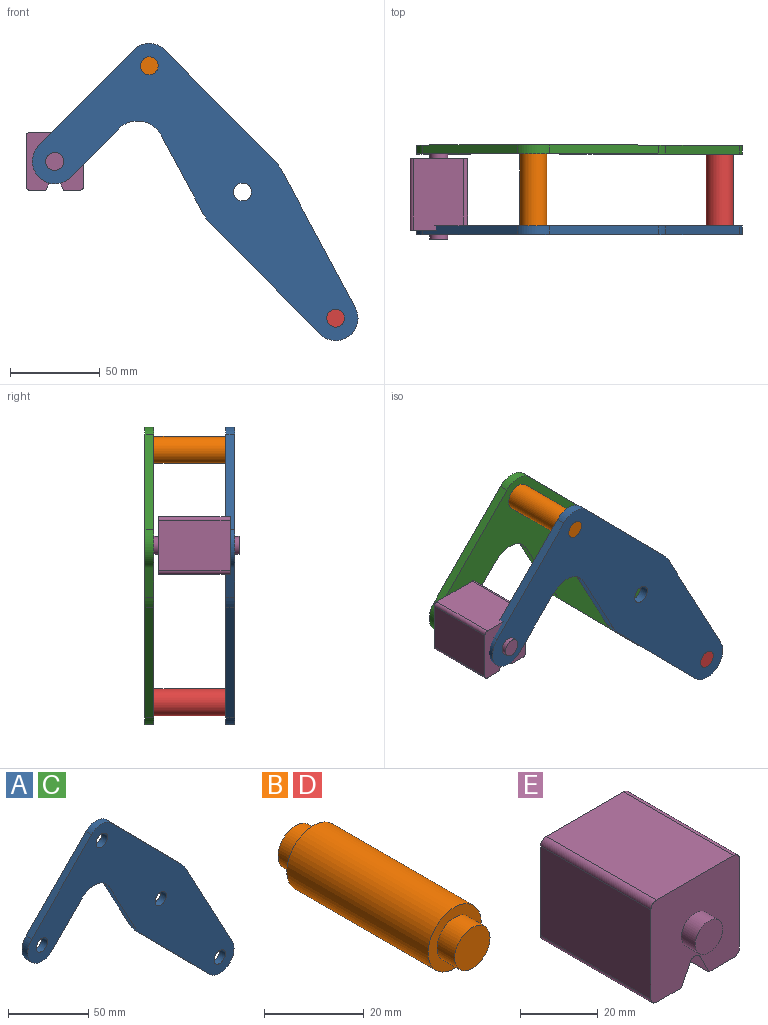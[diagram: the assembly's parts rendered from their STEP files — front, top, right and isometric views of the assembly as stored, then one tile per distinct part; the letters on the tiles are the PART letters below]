
ASSEMBLY  parts=5 mates=5
PART A: 18 faces, bbox 181.7x5x165.8 mm
  f0: plane 43.49x23.35mm, normal (-0.88,0,-0.47), area 246.8mm2, adj f1,f14,f16,f17
  f1: cylinder r=25mm len=5.75mm, axis (0,1,0), area 35.8mm2, adj f0,f2,f16,f17
  f2: plane 61.6x60.87mm, normal (-0.71,0,-0.7), area 433mm2, adj f1,f3,f16,f17
  f3: cylinder r=12.5mm len=21.39mm, axis (0,1,0), area 178.4mm2, adj f2,f4,f16,f17
  f4: plane 76.3x40.96mm, normal (0.88,0,0.47), area 433mm2, adj f3,f5,f16,f17
  f5: cylinder r=25mm len=5.75mm, axis (0,1,0), area 35.8mm2, adj f4,f6,f16,f17
  f6: plane 61.6x60.87mm, normal (0.71,0,0.7), area 433mm2, adj f5,f7,f16,f17
  f7: cylinder r=12.5mm len=17.78mm, axis (0,1,0), area 98.9mm2, adj f6,f8,f16,f17
  f8: plane 53.35x52.71mm, normal (-0.71,0,0.7), area 375mm2, adj f7,f9,f16,f17
  f9: cylinder r=12.5mm len=21.39mm, axis (0,1,0), area 196.3mm2, adj f8,f10,f16,f17
  f10: plane 26.86x26.54mm, normal (0.71,0,-0.7), area 188.8mm2, adj f9,f14,f16,f17
  f11: cylinder r=5mm len=10mm, axis (0,1,0), area 157.1mm2, adj f16,f17
  f12: cylinder r=5mm len=10mm, axis (0,1,0), area 157.1mm2, adj f16,f17
  f13: cylinder r=5mm len=10mm, axis (0,1,0), area 157.1mm2, adj f16,f17
  f14: cylinder r=15mm len=23.89mm, axis (0,1,0), area 140.2mm2, adj f0,f10,f16,f17
  f15: cylinder r=5mm len=10mm, axis (0,1,0), area 157.1mm2, adj f16,f17
  f16: plane 181.66x165.78mm, normal (0,-1,0), area 8710.1mm2, adj f0,f1,f2,f3,f4,f5,f6,f7
  f17: plane 181.66x165.78mm, normal (0,1,0), area 8710.1mm2, adj f0,f1,f2,f3,f4,f5,f6,f7
PART B: 7 faces, bbox 15x50x15 mm
  f0: cylinder r=7.5mm len=40mm, axis (0,-1,0), area 1885mm2, adj f2,f5
  f1: cylinder r=5mm len=10mm, axis (0,1,0), area 157.1mm2, adj f2,f3
  f2: plane 15x15mm, normal (0,-1,0), area 98.2mm2, adj f0,f1
  f3: plane 10x10mm, normal (0,-1,0), area 78.5mm2, adj f1
  f4: cylinder r=5mm len=10mm, axis (0,-1,0), area 157.1mm2, adj f5,f6
  f5: plane 15x15mm, normal (0,1,0), area 98.2mm2, adj f0,f4
  f6: plane 10x10mm, normal (0,1,0), area 78.5mm2, adj f4
PART C: same geometry as A
PART D: same geometry as B
PART E: 18 faces, bbox 32.1x50x32.1 mm
  f0: plane 40x28.08mm, normal (1,0,0), area 1123.1mm2, adj f4,f10,f13,f14
  f1: plane 40x9.04mm, normal (0,0,-1), area 361.6mm2, adj f2,f4,f10,f14
  f2: plane 40x6.42mm, normal (-0.89,0,-0.45), area 287.2mm2, adj f1,f4,f10,f15
  f3: plane 40x6.42mm, normal (0.89,0,-0.45), area 287.2mm2, adj f4,f5,f10,f15
  f4: plane 32.08x32.08mm, normal (0,-1,0), area 900.6mm2, adj f0,f1,f2,f3,f5,f6,f7,f9
  f5: plane 40x9.04mm, normal (0,0,-1), area 361.6mm2, adj f3,f4,f10,f16
  f6: plane 40x28.08mm, normal (0,0,1), area 1123.1mm2, adj f4,f10,f13,f17
  f7: plane 40x28.08mm, normal (-1,0,0), area 1123.1mm2, adj f4,f10,f16,f17
  f8: plane 10x10mm, normal (0,-1,0), area 78.5mm2, adj f9
  f9: cylinder r=5mm len=10mm, axis (0,1,0), area 157.1mm2, adj f4,f8
  f10: plane 32.08x32.08mm, normal (0,1,0), area 900.6mm2, adj f0,f1,f2,f3,f5,f6,f7,f12
  f11: plane 10x10mm, normal (0,1,0), area 78.5mm2, adj f12
  f12: cylinder r=5mm len=10mm, axis (0,-1,0), area 157.1mm2, adj f10,f11
  f13: cylinder r=2mm len=40mm, axis (0,1,0), area 125.7mm2, adj f0,f4,f6,f10
  f14: cylinder r=2mm len=40mm, axis (0,-1,0), area 125.7mm2, adj f0,f1,f4,f10
  f15: cylinder r=2mm len=40mm, axis (0,1,0), area 177.1mm2, adj f2,f3,f4,f10
  f16: cylinder r=2mm len=40mm, axis (0,1,0), area 125.7mm2, adj f4,f5,f7,f10
  f17: cylinder r=2mm len=40mm, axis (0,-1,0), area 125.7mm2, adj f4,f6,f7,f10
PLACE A at identity fixed
PLACE B at identity
PLACE C t=(0,45,0)mm
PLACE D t=(103.95,0,-140.78)mm
PLACE E t=(0,-2.5,0)mm
MATE revolute C.f7 <-> B.f0  axis (0,1,0) through (-51.98,40,70.39)mm
MATE fastened D.f0 <-> C.f3  axis (0,-1,0) through (51.98,42.5,-70.39)mm
MATE revolute B.f0 <-> A.f7  axis (0,1,0) through (-51.98,-2.5,70.39)mm
MATE revolute E.f9 <-> A.f9  axis (0,1,0) through (-104.69,-2.5,17.04)mm
MATE fastened A.f3 <-> D.f0  axis (0,1,0) through (51.98,-2.5,-70.39)mm
